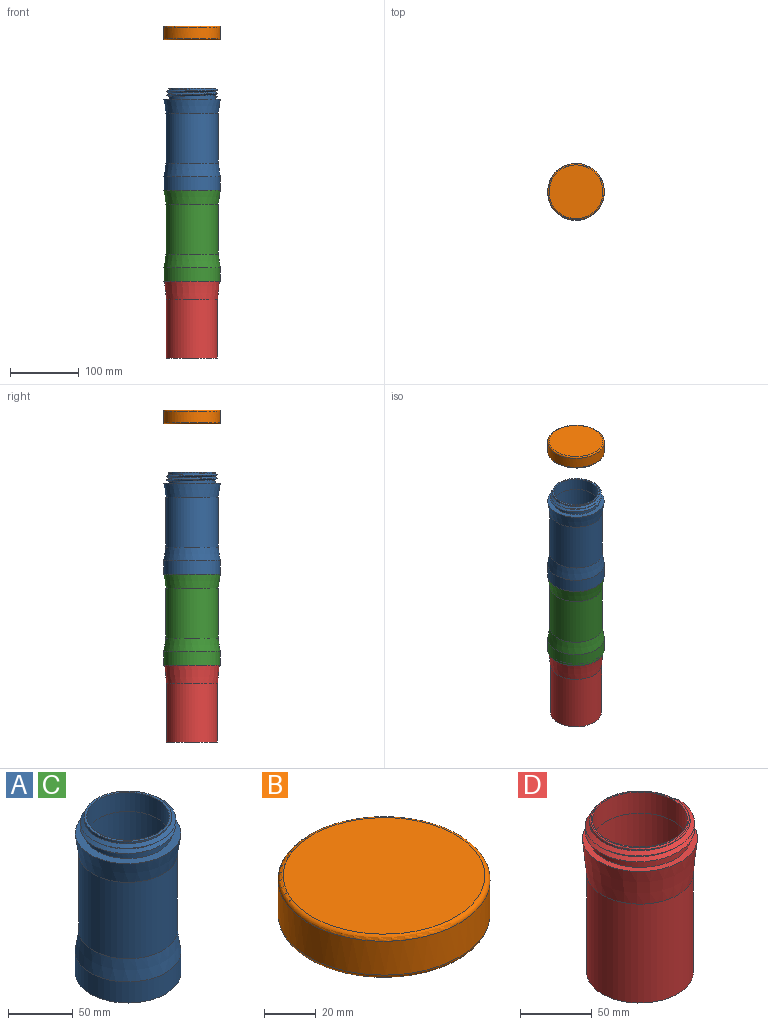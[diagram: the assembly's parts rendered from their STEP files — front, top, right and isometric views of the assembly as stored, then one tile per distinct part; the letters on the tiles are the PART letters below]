
ASSEMBLY  parts=4 mates=3
PART A: 29 faces, bbox 82x90.1x148 mm
  f0: cylinder r=34mm len=68mm, axis (0,0,1), area 854.5mm2, adj f1,f17,f26,f28
  f1: cylinder r=34mm len=68mm, axis (0,0,1), area 106.8mm2, adj f0,f2,f27,f28
  f2: cylinder r=34mm len=68mm, axis (0,0,1), area 534.1mm2, adj f1,f18,f25,f27
  f3: cylinder r=36mm len=110mm, axis (0,0,1), area 24881.4mm2, adj f4,f20
  f4: plane 72x72mm, normal (0,0,1), area 1244.1mm2, adj f3,f5
  f5: cylinder r=30mm len=60mm, axis (0,0,1), area 565.5mm2, adj f4,f6
  f6: torus R=31mm, axis (0,0,1), area 611.9mm2, adj f5,f7
  f7: cylinder r=32mm len=64mm, axis (0,0,1), area 201.1mm2, adj f6,f8
  f8: plane 78x78mm, normal (0,0,-1), area 1561.4mm2, adj f7,f11
  f9: cylinder r=39mm len=78mm, axis (0,0,1), area 612.6mm2, adj f10,f12,f21,f24
  f10: cylinder r=39mm len=78mm, axis (0,0,1), area 122.5mm2, adj f9,f11,f23,f24
  f11: cylinder r=39mm len=78mm, axis (0,0,1), area 1470.3mm2, adj f8,f10,f22,f23
  f12: plane 82x82mm, normal (0,0,-1), area 502.7mm2, adj f9,f13
  f13: cylinder r=41mm len=82mm, axis (0,0,1), area 5152.2mm2, adj f12,f14
  f14: cone r=41mm half-angle=8.6deg, axis (0,0,-1), area 4963.7mm2, adj f13,f15
  f15: cylinder r=38mm len=76mm, axis (0,0,1), area 17298.8mm2, adj f14,f16
  f16: cone r=41mm half-angle=8.6deg, axis (0,0,1), area 4963.7mm2, adj f15,f17
  f17: plane 82x82mm, normal (0,0,1), area 1649.3mm2, adj f0,f16
  f18: plane 68x68mm, normal (0,0,1), area 414.7mm2, adj f2,f19
  f19: cylinder r=32mm len=64mm, axis (0,0,1), area 3619.1mm2, adj f18,f20
  f20: plane 72x72mm, normal (0,0,-1), area 854.5mm2, adj f3,f19
  f21: plane 4.5x3mm, normal (0,-1,0), area 6.8mm2, adj f9,f23,f24
  f22: plane 4.5x3mm, normal (0,1,0), area 6.8mm2, adj f11,f23,f24
  f23: bspline ~90.07x78mm, area 1767.4mm2, adj f10,f11,f21,f22,f24
  f24: bspline ~90.07x78mm, area 1767.7mm2, adj f9,f10,f21,f22,f23
  f25: plane 4.5x3mm, normal (0,1,0), area 6.8mm2, adj f2,f27,f28
  f26: plane 4.5x3mm, normal (0,-1,0), area 6.7mm2, adj f0,f27,f28
  f27: bspline ~85.45x74mm, area 1673.1mm2, adj f1,f2,f25,f26,f28
  f28: bspline ~85.45x74mm, area 1673.5mm2, adj f0,f1,f25,f26,f27
PART B: 16 faces, bbox 88.8x90.1x20 mm
  f0: plane 60x60mm, normal (0,0,-1), area 2827.4mm2, adj f1
  f1: cylinder r=30mm len=60mm, axis (0,0,1), area 188.5mm2, adj f0,f2
  f2: torus R=31mm, axis (0,0,1), area 611.9mm2, adj f1,f3
  f3: cylinder r=32mm len=64mm, axis (0,0,1), area 201.1mm2, adj f2,f4
  f4: plane 78x78mm, normal (0,0,-1), area 1561.4mm2, adj f3,f7
  f5: cylinder r=39mm len=78mm, axis (0,0,1), area 612.6mm2, adj f6,f10,f13,f14
  f6: cylinder r=39mm len=78mm, axis (0,0,1), area 122.5mm2, adj f5,f7,f12,f13
  f7: cylinder r=39mm len=78mm, axis (0,0,1), area 1470.3mm2, adj f4,f6,f11,f12
  f8: cylinder r=41mm len=82mm, axis (0,0,1), area 4121.8mm2, adj f14,f15
  f9: plane 78x78mm, normal (0,0,1), area 4778.4mm2, adj f15
  f10: plane 4.5x3mm, normal (0,-1,0), area 6.8mm2, adj f5,f12,f13
  f11: plane 4.5x3mm, normal (0,1,0), area 6.8mm2, adj f7,f12,f13
  f12: bspline ~90.07x78mm, area 1767.4mm2, adj f6,f7,f10,f11,f13
  f13: bspline ~90.07x78mm, area 1767.7mm2, adj f5,f6,f10,f11,f12
  f14: torus R=39mm, axis (0,0,1), area 795mm2, adj f5,f8
  f15: torus R=39mm, axis (0,0,-1), area 795mm2, adj f8,f9
PART C: same geometry as A
PART D: 17 faces, bbox 80.3x88.1x131.1 mm
  f0: cylinder r=37mm len=84.15mm, axis (0,0,-1), area 19563.1mm2, adj f1,f11
  f1: cone r=40mm half-angle=5.7deg, axis (0,0,1), area 7257.1mm2, adj f0,f2
  f2: plane 80x80mm, normal (0,0,1), area 1178.1mm2, adj f1,f3
  f3: cylinder r=35mm len=70mm, axis (0,0,-1), area 934.6mm2, adj f2,f4,f13,f14,f15
  f4: cylinder r=35mm len=70mm, axis (0,0,-1), area 357.2mm2, adj f3,f5,f12,f14,f15,f16
  f5: cylinder r=35mm len=45.5mm, axis (0,0,-1), area 49.3mm2, adj f4,f14,f16
  f6: plane 69.3x68.3mm, normal (0,0,1), area 226.7mm2, adj f7,f12,f14,f16
  f7: cylinder r=33mm len=66mm, axis (0,0,-1), area 3732.2mm2, adj f6,f8
  f8: plane 70x70mm, normal (0,0,-1), area 427.3mm2, adj f7,f9
  f9: cylinder r=35mm len=110mm, axis (0,0,-1), area 24190.3mm2, adj f8,f10
  f10: plane 70x70mm, normal (0,0,1), area 3848.5mm2, adj f9
  f11: plane 74x74mm, normal (0,0,-1), area 4300.8mm2, adj f0
  f12: plane 4.5x4mm, normal (0,1,0), area 7mm2, adj f4,f6,f14,f15,f16
  f13: plane 4.5x3mm, normal (0,-1,0), area 6.8mm2, adj f3,f14,f15
  f14: bspline ~87.76x76mm, area 1733.1mm2, adj f3,f4,f5,f6,f12,f13,f15,f16
  f15: bspline ~87.76x76mm, area 1720.6mm2, adj f3,f4,f12,f13,f14
  f16: torus R=34mm, axis (0,0,1), area 282.9mm2, adj f4,f5,f6,f12,f14
PLACE A t=(1.2,6.97,260.54)mm
PLACE B rot(axis=(0,0,1),72.5deg) t=(-26.04,44.16,479.09)mm
PLACE C t=(1.2,6.97,128.54)mm
PLACE D t=(-2.8,6.97,1.54)mm fixed
MATE cylindrical D.f0 <-> B.f1  axis (0,0,1) through (-37.8,6.97,113.54)mm
MATE cylindrical C.f0 <-> D.f0  axis (0,0,-1) through (-37.8,6.97,110.54)mm
MATE cylindrical C.f0 <-> A.f0  axis (0,0,1) through (-37.8,6.97,242.54)mm
